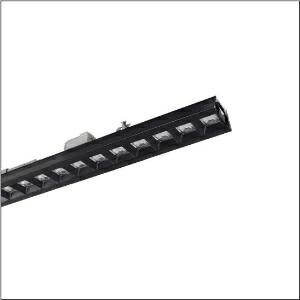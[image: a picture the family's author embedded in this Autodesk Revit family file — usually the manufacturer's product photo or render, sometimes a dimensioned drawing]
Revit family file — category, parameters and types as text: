
# Revit family: licross_r__21_silica_51ts12dn4zm00582xx_af91
name_source: partatom
category: Lighting Fixtures
units: mm (PartAtom-declared; Revit-internal decimal feet)

## family parameters
Cut with Voids When Loaded = No
Host = Face
Light Source = No
Part Type = Normal
Room Calculation Point = No
Round Connector Dimension = Use Diameter
Shared = No

## types (1)
- --- (1 x LED, 6340 lm, 39 W, 4000K)
    Apparent Load = 39 VA
    CIE Flux Codes = 86 100 100 100 100
    Color Rendering = 80
    Color Temperature = 4000K
    Default Elevation = 1800 mm
    Description = Licross® 21 Silica, luminaire insert, of sheet steel, galvanised, black, length: 1.500mm, width: 82mm, height: 86mm, LED rated luminous flux: 6.340lm, light colour: 840, control gear: DALI 2, with plug, 5-pole, with phase selection, mains connection: 220..240V, AC, 50/60Hz, rated input power: 39W, halogen-free wiring, primary light control with lens, of PMMA, primary anti-glare with darklight reflector, of PC, CAT 2 (L<= 1000cd/m²), light emission: direct distribution, primary light characteristic: symmetric, protection rating (complete): IP40, insulation class (complete): insulation class I (protective earthing), certification: CE, UKCA, protection symbol: D if used in an environment without relevant dust loads, impact resistance: IK03, permissible ambient temperature for indoor applications: -25..+45°C, corresponds to IFS (International Featured Standards) requirements for safety and quality in the food industry, reducing of maximum allowable ambient temperature of 5°C with ceiling mounting, LABS conformity tested according to VDMA 24364:2018-05, packaging unit: 1 piece
    Height = 86 mm
    Lamp = 1 x LED
    Lamp Light Flux = 6340 lm
    Lamp Power = 39 W
    Lamp count = 1
    Length = 1500 mm
    Luminous efficacy = 163 lm/W
    Manufacturer = Siteco
    ModVariant = No
    Model = 51TS12DN4ZM00582XX
    Mounting Place = Ceiling
    Mounting Type = Pendant
    Number of Poles = 1
    OnlyDefault = Yes
    Power Factor = 1
    Product Name = Licross® 21 Silica
    Product group = luminaire insert
    ProductGroupID = 901
    Protection Class = Protection class I
    Protection Degree = IP 40
    RLX_Detail_Level = 1
    RLX_Emergency_Light_Flux = 0 lm
    RLX_Emergency_Type = 0
    RLX_Emergency_Type_DB = No
    RlxData = <blob elided: 56377 chars, md5=264402ca>
    Socket = socket
    Standby Power = 0 W
    System Light Flux = 6340 lm
    System Power = 39 W
    Type Comments = factory setting: luminous flux: 100 % | dim-lin: 254 | 435 mA
    Type Image = l_1290829.jpg
    URL = http://relux.com
    VarID = @adj_054721
    Voltage = 0 V
    Weight = 0.00 kg
    Width = 82 mm  [stored 0.269029 ft]

note: [stored X ft] marks values corroborated as IEEE doubles in the binary element streams (Revit-internal decimal feet)

## geometry (parser evidence)
native form markers: Blend x4, Sweep x11
no freeform markers — native parametric forms only
